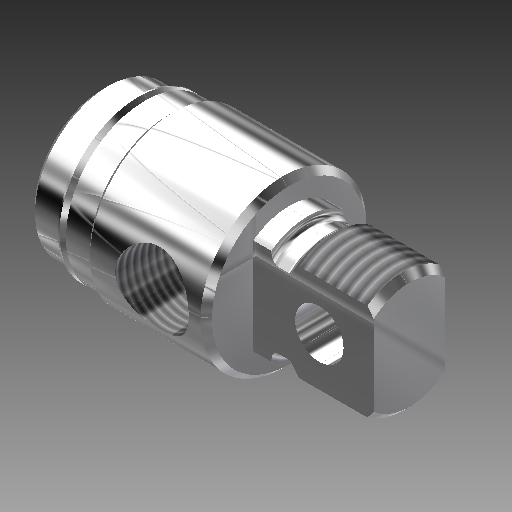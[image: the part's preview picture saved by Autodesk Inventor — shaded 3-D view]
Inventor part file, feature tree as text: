
AUTODESK INVENTOR PART (.ipt)
format: ipt  version: 2017 (Build 210142000, 142)  size: 381,440 bytes
history: native  units: in
note: dims shown in document units (in); Inventor stores cm internally (conversion verified against a paired STEP export)
features: other x154, sketch x7, revolve x4, thread x2, extrude x2, hole x1
ambient origin geometry x8: Origin, YZ Plane, XZ Plane, XY Plane, X Axis, Y Axis, Z Axis, Center Point
bodies: Solid1 (feature_tree)
feature tree (170):
  revolve  "Revolution1"  Angle=360.0deg
  revolve  "Revolution2"  [1 undecoded]
  thread  "Thread1"  [1 undecoded]
  extrude  "Extrusion1"  TaperAngle=360.0deg  [1 undecoded]
  hole  "Hole1"  [1 undecoded]
  revolve  "Revolution3"  [1 undecoded]
  thread  "Thread2"  [1 undecoded]
  revolve  "Revolution4"  [1 undecoded]
  extrude  "Extrusion2"  [1 undecoded]
  other  "1_XY"
  other  "1_YZ"
  other  "1_ZX"
  other  "1_X"
  other  "1_Y"
  other  "1_Z"
  other  "1_Center"
  other  "c1_XY"
  other  "c1_YZ"
  other  "c1_ZX"
  other  "c1_X"
  other  "c1_Y"
  other  "c1_Z"
  other  "c1_Center"
  other  "c2_XY"
  other  "c2_YZ"
  other  "c2_ZX"
  other  "c2_X"
  other  "c2_Y"
  other  "c2_Z"
  other  "c2_Center"
  other  "cc1_XY"
  other  "cc1_YZ"
  other  "cc1_ZX"
  other  "cc1_X"
  other  "cc1_Y"
  other  "cc1_Z"
  other  "cc1_Center"
  other  "cc2_XY"
  other  "cc2_YZ"
  other  "cc2_ZX"
  other  "cc2_X"
  other  "cc2_Y"
  other  "cc2_Z"
  other  "cc2_Center"
  other  "lovra1_XY"
  other  "lovra1_YZ"
  other  "lovra1_ZX"
  other  "lovra1_X"
  other  "lovra1_Y"
  other  "lovra1_Z"
  other  "lovra1_Center"
  other  "lovra2_XY"
  other  "lovra2_YZ"
  other  "lovra2_ZX"
  other  "lovra2_X"
  other  "lovra2_Y"
  other  "lovra2_Z"
  other  "lovra2_Center"
  other  "lovra21_XY"
  other  "lovra21_YZ"
  other  "lovra21_ZX"
  other  "lovra21_X"
  other  "lovra21_Y"
  other  "lovra21_Z"
  other  "lovra21_Center"
  other  "lovra22_XY"
  other  "lovra22_YZ"
  other  "lovra22_ZX"
  other  "lovra22_X"
  other  "lovra22_Y"
  other  "lovra22_Z"
  other  "lovra22_Center"
  other  "lovra3_XY"
  other  "lovra3_YZ"
  other  "lovra3_ZX"
  other  "lovra3_X"
  other  "lovra3_Y"
  other  "lovra3_Z"
  other  "lovra3_Center"
  other  "olen_XY"
  other  "olen_YZ"
  other  "olen_ZX"
  other  "olen_X"
  other  "olen_Y"
  other  "olen_Z"
  other  "olen_Center"
  other  "p1_XY"
  other  "p1_YZ"
  other  "p1_ZX"
  other  "p1_X"
  other  "p1_Y"
  other  "p1_Z"
  other  "p1_Center"
  other  "p2_XY"
  other  "p2_YZ"
  other  "p2_ZX"
  other  "p2_X"
  other  "p2_Y"
  other  "p2_Z"
  other  "p2_Center"
  other  "port_XY"
  other  "port_YZ"
  other  "port_ZX"
  other  "port_X"
  other  "port_Y"
  other  "port_Z"
  other  "port_Center"
  other  "port2_XY"
  other  "port2_YZ"
  other  "port2_ZX"
  other  "port2_X"
  other  "port2_Y"
  other  "port2_Z"
  other  "port2_Center"
  other  "thd1_XY"
  other  "thd1_YZ"
  other  "thd1_ZX"
  other  "thd1_X"
  other  "thd1_Y"
  other  "thd1_Z"
  other  "thd1_Center"
  other  "thd2_XY"
  other  "thd2_YZ"
  other  "thd2_ZX"
  other  "thd2_X"
  other  "thd2_Y"
  other  "thd2_Z"
  other  "thd2_Center"
  other  "to_mounting_bracket_XY"
  other  "to_mounting_bracket_YZ"
  other  "to_mounting_bracket_ZX"
  other  "to_mounting_bracket_X"
  other  "to_mounting_bracket_Y"
  other  "to_mounting_bracket_Z"
  other  "to_mounting_bracket_Center"
  other  "to_nut_XY"
  other  "to_nut_YZ"
  other  "to_nut_ZX"
  other  "to_nut_X"
  other  "to_nut_Y"
  other  "to_nut_Z"
  other  "to_nut_Center"
  other  "to_pin_XY"
  other  "to_pin_YZ"
  other  "to_pin_ZX"
  other  "to_pin_X"
  other  "to_pin_Y"
  other  "to_pin_Z"
  other  "to_pin_Center"
  other  "to_screw_XY"
  other  "to_screw_YZ"
  other  "to_screw_ZX"
  other  "to_screw_X"
  other  "to_screw_Y"
  other  "to_screw_Z"
  other  "to_screw_Center"
  other  "to_tube_XY"
  other  "to_tube_YZ"
  other  "to_tube_ZX"
  other  "to_tube_X"
  other  "to_tube_Y"
  other  "to_tube_Z"
  other  "to_tube_Center"
  sketch  "Sketch_8"  dims[d2=0.3547in d3=0.0in d4=0.625in d5=0.0in]
  sketch  "Sketch_15"  dims[d14=0.3021in d15=0.0in d16=360.0deg]
  sketch  "Sketch_9"  dims[d6=0.312in d7=0.75in d8=0.375in d9=0.25in d10=0.5635in d11=0.9284in d12=120.0deg d13=360.0deg]
  sketch  "Sketch4"  dims[d0=360.0deg d1=360.0deg]
  sketch  "Sketch_68"
  sketch  "Sketch_24"  dims[d17=0.5587in d18=0.0in d19=0.0in d20=0.0in d21=0.0in d22=0.0in]
  sketch  "Sketch_43"
note: 8 required parameter values undecoded (feature->parameter linkage not recoverable at this tier; creation-order binding heuristic only, values carry confidence <= 0.55)